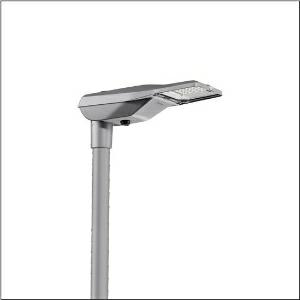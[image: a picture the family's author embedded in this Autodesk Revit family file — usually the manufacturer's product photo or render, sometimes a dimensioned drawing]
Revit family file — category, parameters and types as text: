
# Revit family: streetlight_sl_21_iq_micro___p0_8a_5xe1u31u08cb_c8d0
name_source: partatom
category: Lighting Fixtures
units: mm (PartAtom-declared; Revit-internal decimal feet)

## family parameters
Cut with Voids When Loaded = No
Host = Face
Light Source = No
Part Type = Normal
Room Calculation Point = No
Round Connector Dimension = Use Diameter
Shared = No

## types (1)
- --- (1 x LED, 2890 lm, 19.1 W, 3000K)
    Apparent Load = 19 VA
    CIE Flux Codes = 33 69 96 100 100
    Color Rendering = 70
    Color Temperature = 3000K
    Default Elevation = 1800 mm
    Description = Streetlight SL 21 iQ micro, mast luminaire, primary light control with lens, of PMMA, primary optical cover: cover, of toughened safety glass, transparent, light distribution: P0.8a, light emission: direct distribution, primary light characteristic: asymmetric, installation type: post-top, side-entry, LED, High Power LED, rated luminous flux: 2.890lm, luminous efficacy: 151lm/W, light colour: 730, colour temperature: 3000K, control gear: iQ-Street Remote, D4i with power reduction, control: pre-setting: logarithmic dimming characteristic, Street-Remote, Auto-Match, Temp-Guard, Lumen-Switch, Night-Set, Smart-Wire, Light-Fading, Desk-Remote (wireless, voltage-free reading and setting of iQ features in the workshop via application-optimized NFC function/RFID function), optimised constant luminous flux control (CLO 2.0), mains connection: 220..240V, AC, 50/60Hz, start of lifetime: 19W, end of service life: 20W, reduction: 9W, luminaire housing, of diecast aluminium, powder-coated, Siteco® metallic grey (DB 702S), corrosivity category C5 mid according to DIN EN ISO 12944, please order mast flange separately, inclination adjustable: 0°, 5°, 10°, 15°, sealing non-destructively replaceable, multi-level sealing system, length: 528mm, width: 235mm, height: 110mm, mast flange for spigot size: 42mm (side-entry): 5XC10008XM4, 60/48mm (side-entry/post-top): 5XC10108XM2, 76/60mm (side-entry/post-top): 5XC10108XM1, mounting height: 4..8m, Smart Interface below, protection rating (complete): IP66, insulation class (complete): insulation class II (safety insulation), certification: CE, ENEC, ENEC+, VDE, impact resistance: IK10, permissible operating ambient temperature for outdoor applications: -40..+50°C, standard-compliant lighting for roads and squares, packaging unit: 1 piece

Light Distribution: P0.8a
    Height = 110 mm
    Lamp = 1 x LED
    Lamp Light Flux = 2890 lm
    Lamp Power = 19.1 W
    Lamp count = 1
    Length = 528 mm
    Luminous efficacy = 151 lm/W
    Manufacturer = Siteco
    ModVariant = No
    Model = 5XE1U31U08CB
    Number of Poles = 1
    OnlyDefault = Yes
    Power Factor = 1
    Product Name = Streetlight SL 21 iQ micro | P0.8a
    Product group = mast luminaire | pylon top
    ProductGroupID = 6100
    Protection Class = Protection class II
    Protection Degree = IP 66
    RLX_Detail_Level = 1
    RLX_Emergency_Light_Flux = 0 lm
    RLX_Emergency_Type = 0
    RLX_Emergency_Type_DB = No
    RlxData = <blob elided: 98817 chars, md5=0e93813c>
    Socket = socket
    Standby Power = 0 W
    System Light Flux = 2890 lm
    System Power = 19 W
    Type Comments = factory setting: luminous flux: 100 % | dim-lin: 254 | 387 mA
    Type Image = l_1277290.jpg
    URL = http://relux.com
    VarID = @adj_072966
    Voltage = 0 V
    Weight = 0.00 kg
    Width = 235 mm

## geometry (parser evidence)
native form markers: Blend x4, Sweep x10
no freeform markers — native parametric forms only
